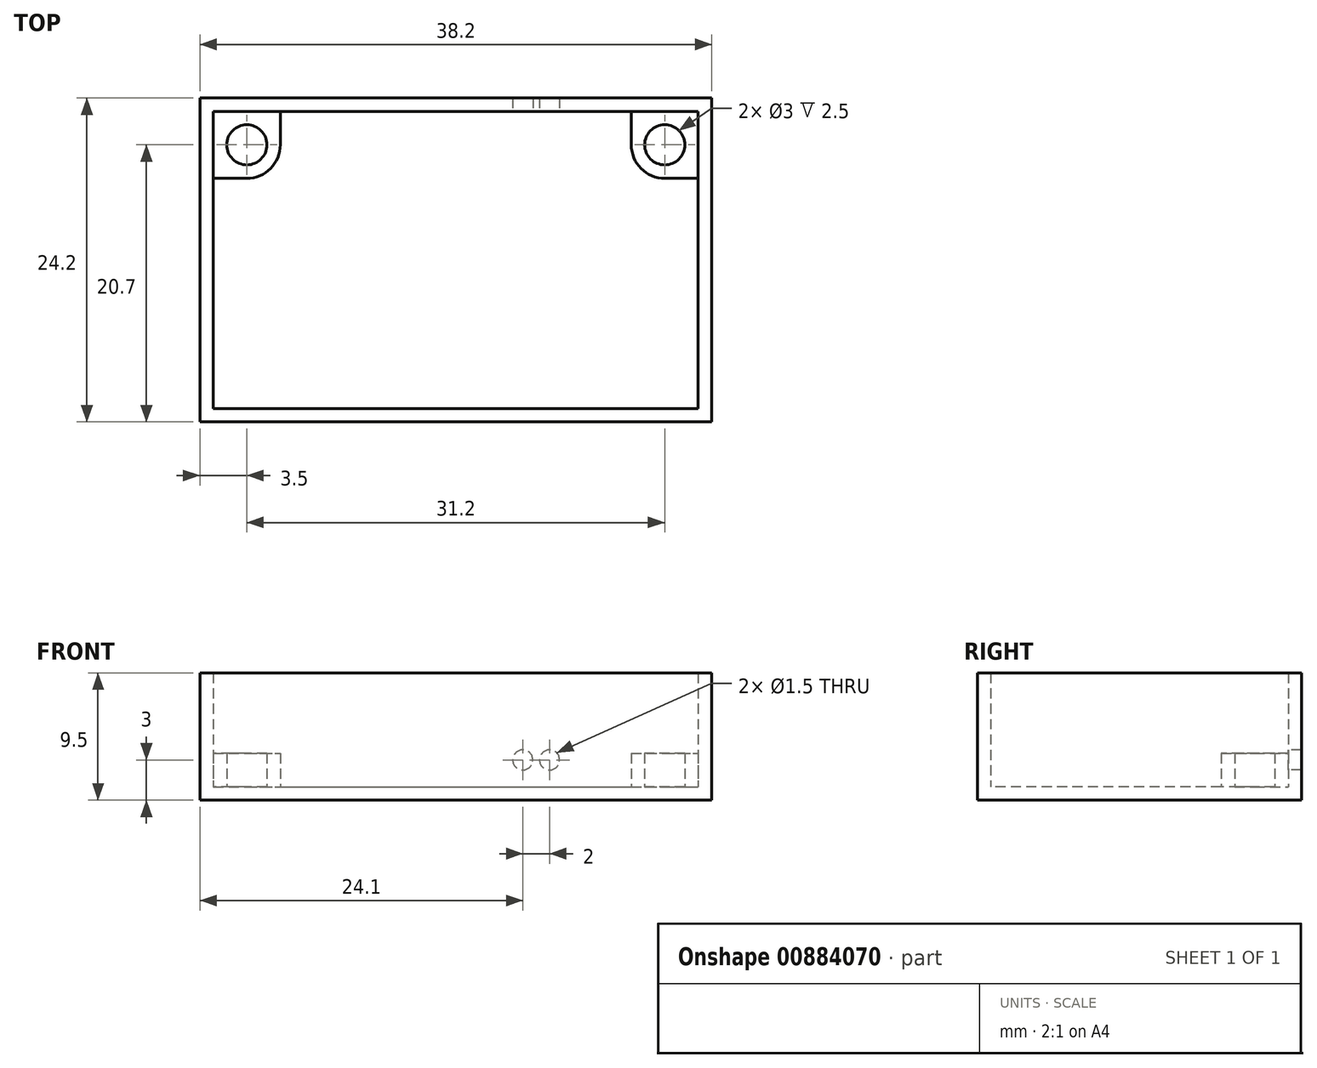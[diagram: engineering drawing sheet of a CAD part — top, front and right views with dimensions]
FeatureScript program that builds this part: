
annotation { "Feature Type Name" : "Feature", "Feature Type Description" : "" }
export const myFeature = defineFeature(function(context is Context, id is Id, definition is map)
    precondition{}
    {
        {
            var Q0;
            Q0=qCreatedBy(makeId("Top.planeOp"),FACE);
            var sketch = newSketch(context, id + "F0", { "sketchPlane" : qUnion([Q0])});
            skLineSegment(sketch, "E0.bottom", {"start": v(-19.1, 12.1) * mm, "end": v(19.1, 12.1) * mm});
            skLineSegment(sketch, "E0.top", {"start": v(-19.1, -12.1) * mm, "end": v(19.1, -12.1) * mm});
            skLineSegment(sketch, "E0.left", {"start": v(-19.1, 12.1) * mm, "end": v(-19.1, -12.1) * mm});
            skLineSegment(sketch, "E0.right", {"start": v(19.1, 12.1) * mm, "end": v(19.1, -12.1) * mm});
            skPoint(sketch, "E0.middle", {"position": v(0, 0) * mm});
            skSolve(sketch);
        }
        {
            var Q0;
            Q0 = qSketchRegion(id + "F0", true);
            extrude(context, id + "F1", {"entities" : qUnion([Q0]), "depth" : 9.5 * mm, "offsetDistance" : 25 * mm});
        }
        {
            var Q0;
            Q0=makeQuery(id+"F1.opExtrude","CAP_FACE",FACE,{"disambiguationData":[OSD([sQuery(id+"F0.wireOp",EDGE,"E0.bottom"),sQuery(id+"F0.wireOp",EDGE,"E0.top"),sQuery(id+"F0.wireOp",EDGE,"E0.left"),sQuery(id+"F0.wireOp",EDGE,"E0.right")])],"isStart":false});
            shell(context, id + "F2", {"entities" : qUnion([Q0]), "thickness" : 1 * mm});
        }
        {
            var Q0;
            Q0=makeQuery(id+"F2.opShell","OFFSET_FACE",FACE,{"disambiguationData":[OSD([sQuery(id+"F0.wireOp",EDGE,"E0.bottom"),sQuery(id+"F0.wireOp",EDGE,"E0.top"),sQuery(id+"F0.wireOp",EDGE,"E0.left"),sQuery(id+"F0.wireOp",EDGE,"E0.right")])]});
            var sketch = newSketch(context, id + "F3", { "sketchPlane" : qUnion([Q0])});
            skCircle(sketch, "E1", {"center": v(-15.6, 8.6) * mm, "radius": 1.5 * mm});
            skLineSegment(sketch, "E2.0", {"start": v(-18.1, 11.1) * mm, "end": v(-18.1, -11.1) * mm, "construction": true});
            skLineSegment(sketch, "E3.0", {"start": v(-18.1, 11.1) * mm, "end": v(18.1, 11.1) * mm, "construction": true});
            skArc(sketch, "E4.0", {"start": v(-15.6, 6.1) * mm, "mid": v(-13.83, 6.83) * mm, "end": v(-13.1, 8.6) * mm});
            skLineSegment(sketch, "E5", {"start": v(-15.6, 6.1) * mm, "end": v(-18.1, 6.1) * mm});
            skLineSegment(sketch, "E6", {"start": v(-13.1, 8.6) * mm, "end": v(-13.1, 11.1) * mm});
            skLineSegment(sketch, "E7.MirrorCS", {"start": v(13.1, 8.6) * mm, "end": v(13.1, 11.1) * mm});
            skArc(sketch, "E8.MirrorCS", {"start": v(15.6, 6.1) * mm, "mid": v(13.83, 6.83) * mm, "end": v(13.1, 8.6) * mm});
            skLineSegment(sketch, "E9.MirrorCS", {"start": v(15.6, 6.1) * mm, "end": v(18.1, 6.1) * mm});
            skCircle(sketch, "E10.MirrorC", {"center": v(15.6, 8.6) * mm, "radius": 1.5 * mm});
            skLineSegment(sketch, "E11", {"start": v(-18.1, 11.1) * mm, "end": v(-13.1, 11.1) * mm});
            skLineSegment(sketch, "E12", {"start": v(-18.1, 6.1) * mm, "end": v(-18.1, 11.1) * mm});
            skLineSegment(sketch, "E13", {"start": v(13.1, 11.1) * mm, "end": v(18.1, 11.1) * mm});
            skLineSegment(sketch, "E14", {"start": v(18.1, 11.1) * mm, "end": v(18.1, 6.1) * mm});
            skSolve(sketch);
        }
        {
            var Q0;
            Q0 = qSketchRegion(id + "F3", true);
            extrude(context, id + "F4", {"entities" : qUnion([Q0]), "operationType" : NewBodyOperationType.ADD, "depth" : 2.5 * mm, "offsetDistance" : 25 * mm});
        }
        {
            var Q0;
            Q0=makeQuery(id+"F2.opShell","OFFSET_FACE",FACE,{"disambiguationData":[OSD([sQuery(id+"F0.wireOp",EDGE,"E0.bottom")])]});
            var sketch = newSketch(context, id + "F5", { "sketchPlane" : qUnion([Q0])});
            skLineSegment(sketch, "E15.0", {"start": v(-13.1, 1) * mm, "end": v(13.1, 1) * mm, "construction": true});
            skCircle(sketch, "E16", {"center": v(5, 3) * mm, "radius": 0.75 * mm});
            skCircle(sketch, "E17", {"center": v(7, 3) * mm, "radius": 0.75 * mm});
            skLineSegment(sketch, "E18", {"start": v(0, 3) * mm, "end": v(12.03, 3) * mm, "construction": true});
            skSolve(sketch);
        }
        {
            var Q0;
            Q0 = qSketchRegion(id + "F5", true);
            var Q1;
            Q1=makeQuery(id+"F1.opExtrude","SWEPT_FACE",FACE,{"disambiguationData":[OSD([sQuery(id+"F0.wireOp",EDGE,"E0.bottom")])]});
            extrude(context, id + "F6", {"entities" : qUnion([Q0]), "operationType" : NewBodyOperationType.REMOVE, "endBound" : BoundingType.UP_TO_SURFACE, "oppositeDirection" : true, "depth" : 25 * mm, "endBoundEntityFace" : qUnion([Q1]), "offsetDistance" : 25 * mm});
        }
    });
